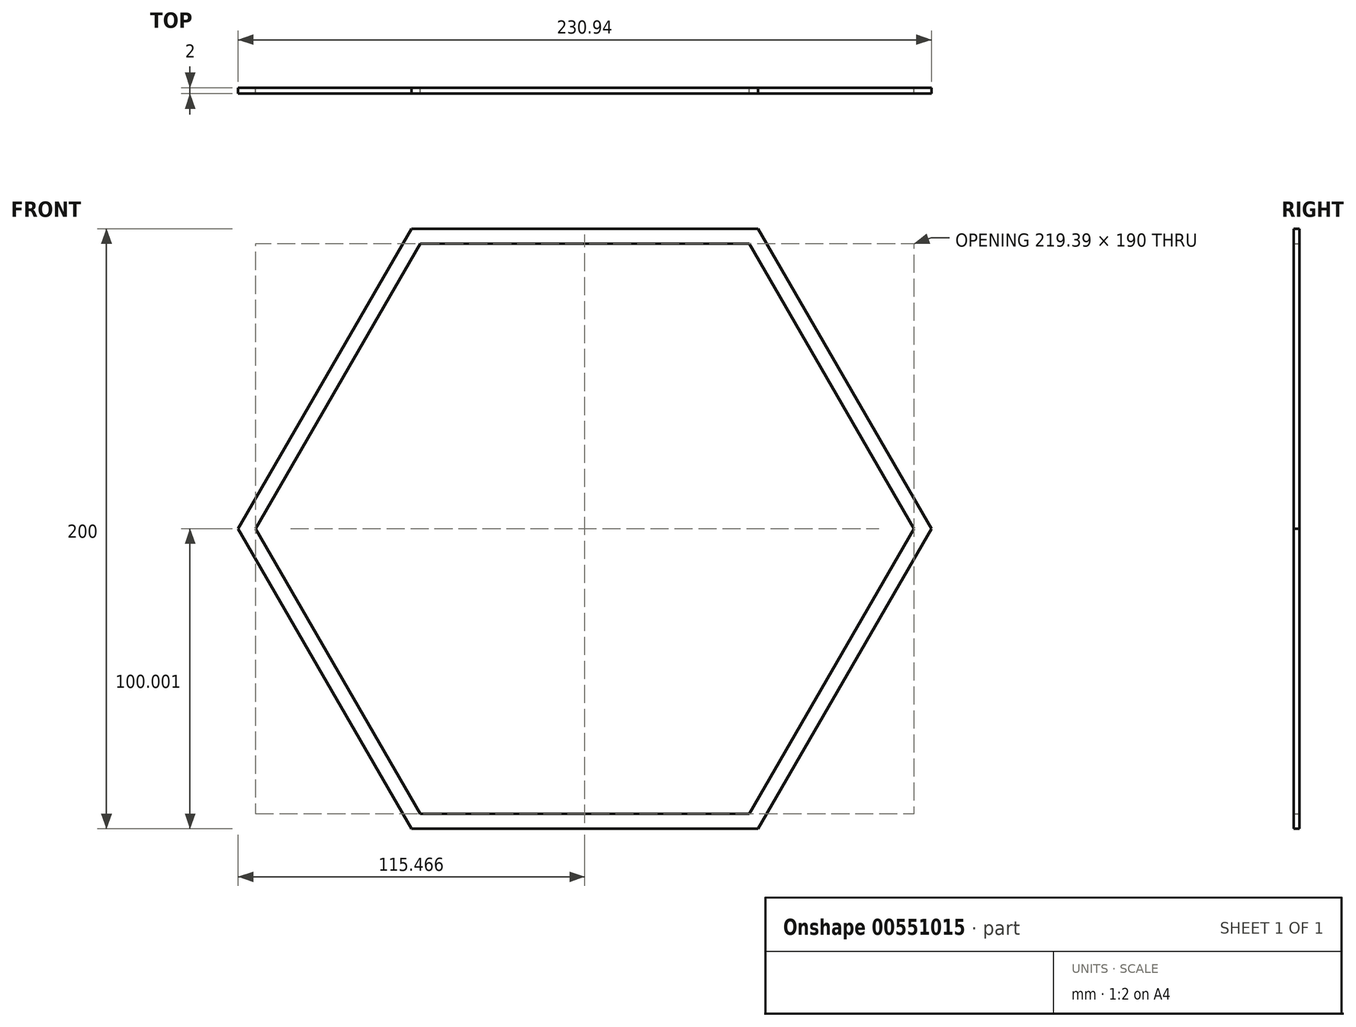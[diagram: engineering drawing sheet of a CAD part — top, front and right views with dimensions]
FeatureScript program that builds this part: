
annotation { "Feature Type Name" : "Feature", "Feature Type Description" : "" }
export const myFeature = defineFeature(function(context is Context, id is Id, definition is map)
    precondition{}
    {
        {
            var Q0;
            Q0=qCreatedBy(makeId("Front.planeOp"),FACE);
            var sketch = newSketch(context, id + "F0", { "sketchPlane" : qUnion([Q0])});
            skCircle(sketch, "E0.cCircle", {"center": v(-33.67, 32.82) * mm, "radius": 100 * mm, "construction": true});
            skLineSegment(sketch, "E0.0", {"start": v(-91.4, 132.82) * mm, "end": v(24.06, 132.82) * mm});
            skLineSegment(sketch, "E0.1", {"start": v(24.06, 132.82) * mm, "end": v(81.8, 32.82) * mm});
            skLineSegment(sketch, "E0.2", {"start": v(81.8, 32.82) * mm, "end": v(24.06, -67.18) * mm});
            skLineSegment(sketch, "E0.3", {"start": v(24.06, -67.18) * mm, "end": v(-91.4, -67.18) * mm});
            skLineSegment(sketch, "E0.4", {"start": v(-91.4, -67.18) * mm, "end": v(-149.14, 32.82) * mm});
            skLineSegment(sketch, "E0.5", {"start": v(-149.14, 32.82) * mm, "end": v(-91.4, 132.82) * mm});
            skPoint(sketch, "E0.0.midPoint", {"position": v(-33.67, 132.82) * mm});
            skLineSegment(sketch, "E1.0", {"start": v(-143.37, 32.82) * mm, "end": v(-88.52, 127.82) * mm});
            skLineSegment(sketch, "E1.1", {"start": v(21.17, 127.82) * mm, "end": v(76.02, 32.82) * mm});
            skLineSegment(sketch, "E1.2", {"start": v(76.02, 32.82) * mm, "end": v(21.17, -62.18) * mm});
            skLineSegment(sketch, "E1.3", {"start": v(-88.52, 127.82) * mm, "end": v(21.17, 127.82) * mm});
            skLineSegment(sketch, "E1.4", {"start": v(21.17, -62.18) * mm, "end": v(-88.52, -62.18) * mm});
            skLineSegment(sketch, "E1.5", {"start": v(-88.52, -62.18) * mm, "end": v(-143.37, 32.82) * mm});
            skSolve(sketch);
        }
        {
            var Q0;
            Q0 = qSketchRegion(id + "F0", true);
            extrude(context, id + "F1", {"entities" : qUnion([Q0]), "depth" : 2 * mm, "offsetDistance" : 25 * mm});
        }
    });
